# Revit family: Lighting-Interior-Pendant_Mount-Manning_Lighting-STILT-LP-572-04-P30
name_source: partatom
category: Lighting Fixtures
revit_build: Autodesk Revit 2013 (Build: 20120221_2030(x64)
units: mm (PartAtom-declared; Revit-internal decimal feet)

## types (1)
- LP-572-04-P30-35
    ADA Compliant = No
    Amperage Estimate = 0 A
    Ballast Factor = 0
    Color Filter = 16777215
    Default Elevation = 4' - 0"
    Dimming Lamp Color Temperature Shift = <None>
    Emit from Line Length = 2' - 0"
    Estimated Fixture Lumens = 2568
    Finish notes = <By Category>
    Frequency = 60 Hz
    Light Source Symbol Size = 3' - 0"
    Lumens per lamp = 892
    Manufacturer = Manning Lighting
    Materials and Finishes = Acrylic
    Mounting Centers = 0' - 0"
    Number of lamps = 4
    Overall Depth = 0' - 0"
    Overall Height = 2' - 0"
    Overall Width = 0' - 4"
    Photometric Web File = Generic
    Primary Lamp Quantity = 4
    Primary Lamp Type = LED ARRAYS
    Recessed Depth = 0' - 0"
    Secondary Lamp quantity = 0
    Separate Switching = Yes
    URL = http://www.manningltg.com
    Unit watts = 30 W
    Voltage = 120 V
    Watts per lamp = 8 W

## geometry (parser evidence)
native form markers: Blend x28, Extrusion x2, Sweep x2
no freeform markers — native parametric forms only
